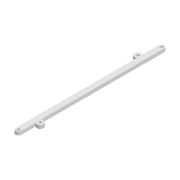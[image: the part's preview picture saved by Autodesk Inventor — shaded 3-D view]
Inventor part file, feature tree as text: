
AUTODESK INVENTOR PART (.ipt)
format: ipt  version: 2022 (Build 260153000, 153)  size: 103,936 bytes
history: native  units: mm
features: extrude x1, sketch x1
ambient origin geometry x8: Origin, YZ Plane, XZ Plane, XY Plane, X Axis, Y Axis, Z Axis, Center Point
bodies: Solid1 (feature_tree)
feature tree (2):
  extrude  "Extrusion1"  Depth=8.0mm
  sketch  "Sketch1"  dims[d0=210.0mm d1=8.0mm d2=4.2mm d3=4.2mm d4=5.0mm d5=0.0mm d6=4.2mm d7=4.2mm d8=3.0mm d9=3.0mm d10=10.0mm d11=10.0mm d12=17.0mm d13=182.0mm]
